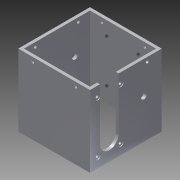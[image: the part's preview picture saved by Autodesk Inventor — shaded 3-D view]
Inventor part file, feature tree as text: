
AUTODESK INVENTOR PART (.ipt)
format: ipt  version: 2013 (Build 170138000, 138)  size: 200,192 bytes
history: native  units: mm
features: sketch x6, hole x5, thread x4, other x1, extrude x1
ambient origin geometry x1: Origin
feature tree (17):
  other  "ソリッド1"
  extrude  "押し出し1"  Depth=50.0mm
  hole  "穴1"  [1 undecoded]
  hole  "穴6"  [1 undecoded]
  hole  "穴12"  [1 undecoded]
  thread  "ねじ1"
  thread  "ねじ2"
  thread  "ねじ3"
  thread  "ねじ4"
  hole  "穴13"  [1 undecoded]
  hole  "穴14"  [1 undecoded]
  sketch  "スケッチ1"
  sketch  "スケッチ3"
  sketch  "スケッチ11"
  sketch  "スケッチ17"
  sketch  "スケッチ18"
  sketch  "スケッチ19"
note: 5 required parameter values undecoded (feature->parameter linkage not recoverable at this tier; creation-order binding heuristic only, values carry confidence <= 0.55)
